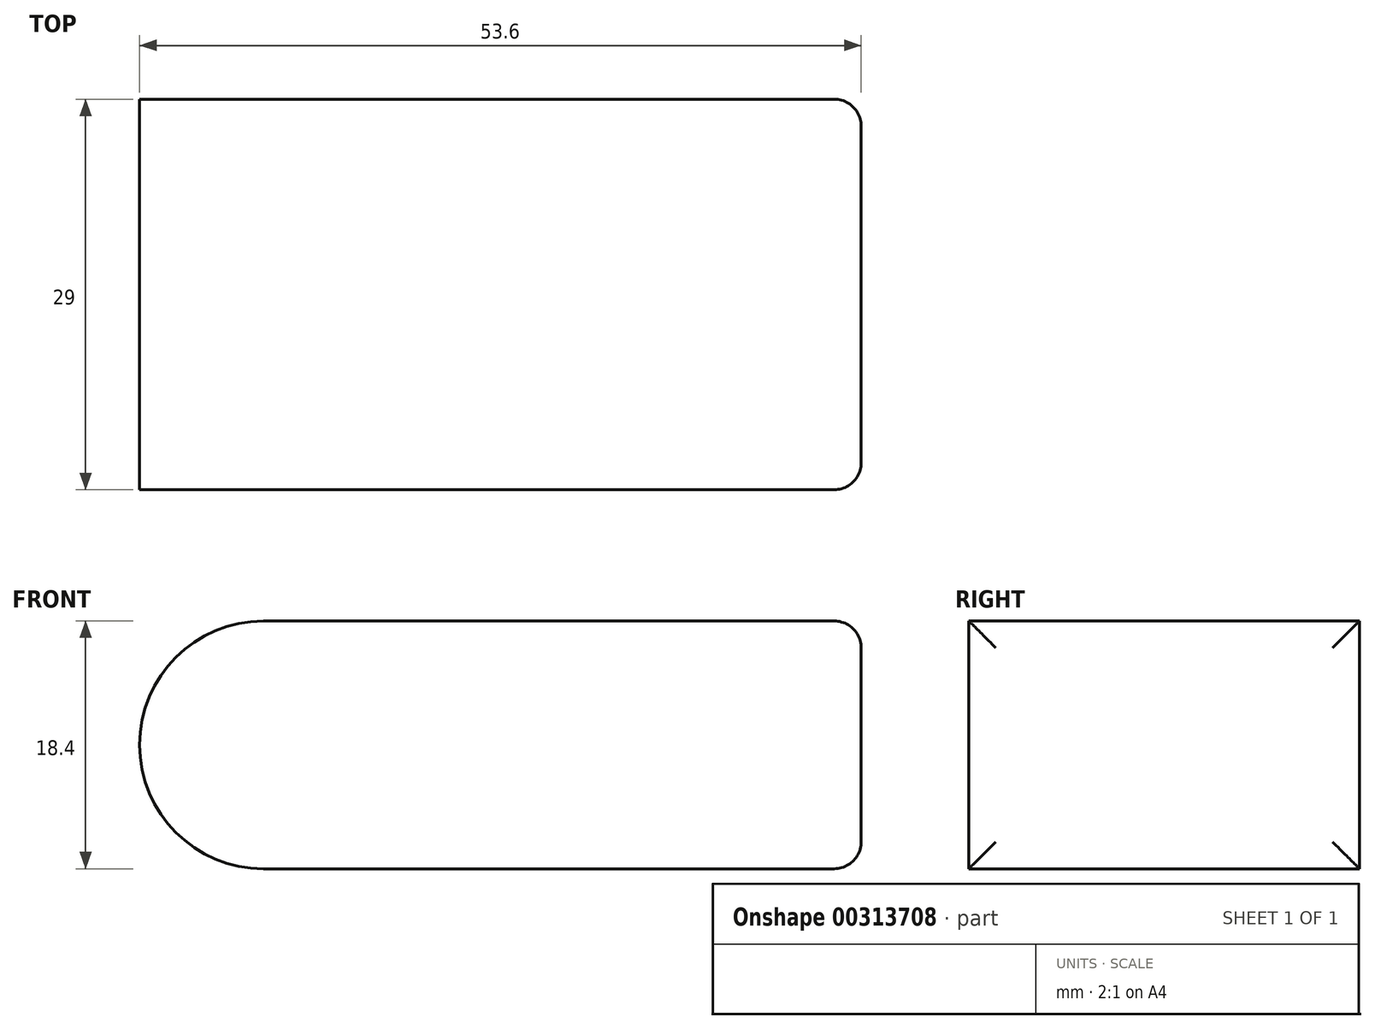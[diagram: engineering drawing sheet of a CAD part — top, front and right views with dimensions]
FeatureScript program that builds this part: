
annotation { "Feature Type Name" : "Feature", "Feature Type Description" : "" }
export const myFeature = defineFeature(function(context is Context, id is Id, definition is map)
    precondition{}
    {
        {
            var Q0;
            Q0=qCreatedBy(makeId("Top.planeOp"),FACE);
            var sketch = newSketch(context, id + "F0", { "sketchPlane" : qUnion([Q0])});
            skLineSegment(sketch, "E0.bottom", {"start": v(-26.8, 14.5) * mm, "end": v(26.8, 14.5) * mm});
            skLineSegment(sketch, "E0.top", {"start": v(-26.8, -14.5) * mm, "end": v(26.8, -14.5) * mm});
            skLineSegment(sketch, "E0.left", {"start": v(-26.8, 14.5) * mm, "end": v(-26.8, -14.5) * mm});
            skLineSegment(sketch, "E0.right", {"start": v(26.8, 14.5) * mm, "end": v(26.8, -14.5) * mm});
            skPoint(sketch, "E0.middle", {"position": v(0, 0) * mm});
            skSolve(sketch);
        }
        {
            var Q0;
            Q0=qSketchRegion(id+"F0",true);
            extrude(context, id + "F1", {"entities" : qUnion([Q0]), "depth" : 18.4 * mm});
        }
        {
            var Q0;
            Q0=makeQuery(id+"F1.opExtrude","CAP_EDGE",EDGE,{"disambiguationData":[OSD([sQuery(id+"F0.wireOp",EDGE,"E0.left")])],"isStart":false});
            var Q1;
            Q1=makeQuery(id+"F1.opExtrude","CAP_EDGE",EDGE,{"disambiguationData":[OSD([sQuery(id+"F0.wireOp",EDGE,"E0.left")])],"isStart":true});
            fillet(context, id + "F2", {"entities" : qUnion([Q0, Q1]), "radius" : 9.2 * mm, "tangentPropagation" : true, "allowEdgeOverflow" : false});
        }
        {
            var Q0;
            Q0=makeQuery(id+"F1.opExtrude","SWEPT_FACE",FACE,{"disambiguationData":[OSD([sQuery(id+"F0.wireOp",EDGE,"E0.right")])]});
            fillet(context, id + "F3", {"entities" : qUnion([Q0]), "radius" : 2 * mm, "tangentPropagation" : true, "allowEdgeOverflow" : false});
        }
    });
